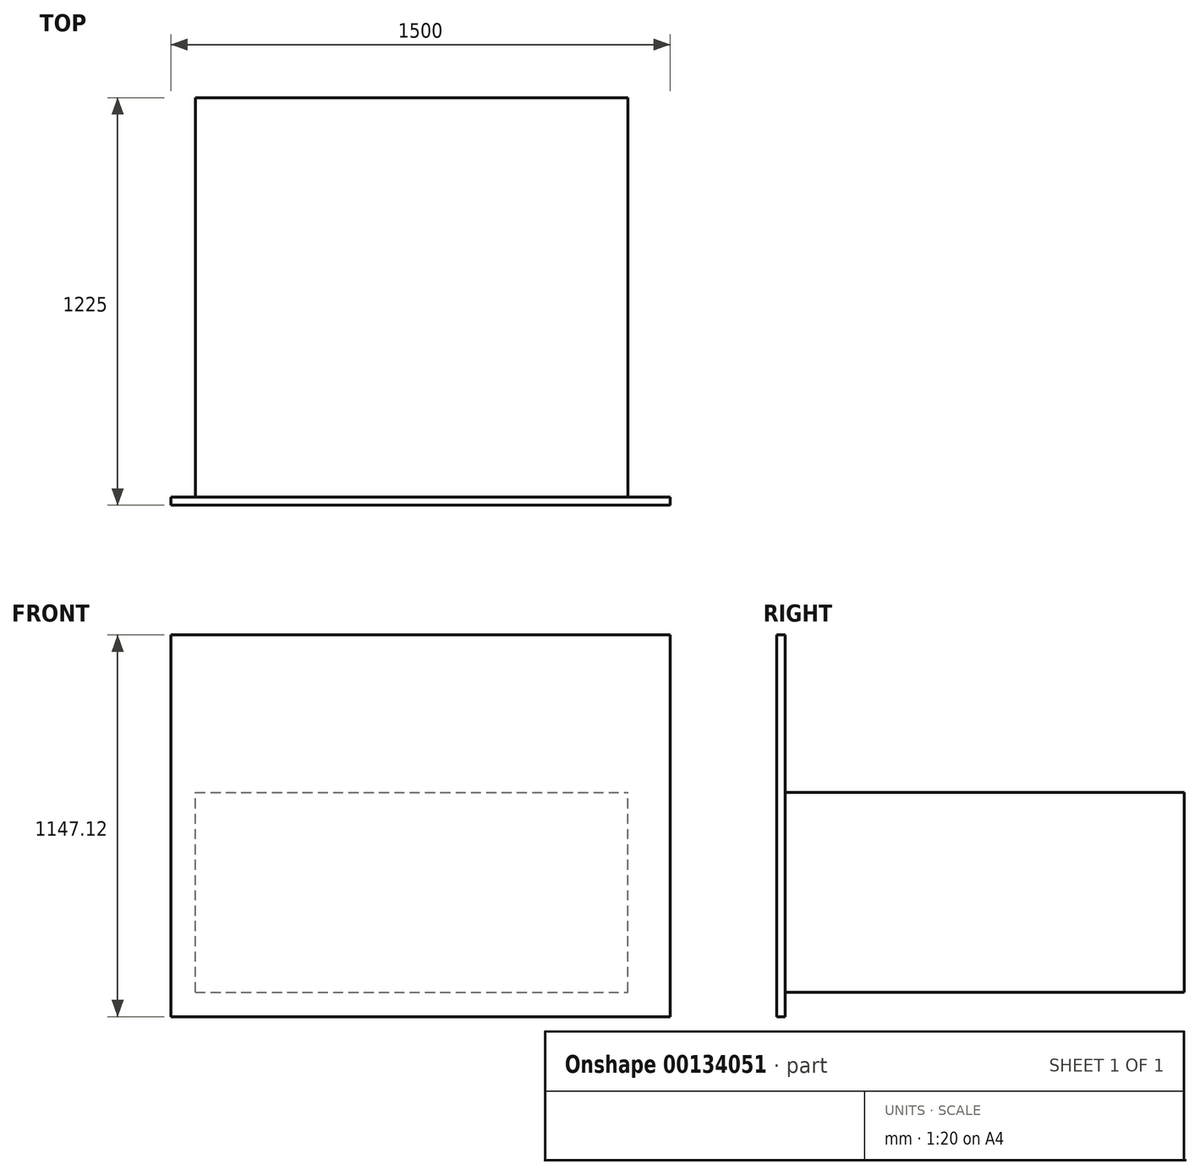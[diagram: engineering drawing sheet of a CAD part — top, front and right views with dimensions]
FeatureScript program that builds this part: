
annotation { "Feature Type Name" : "Feature", "Feature Type Description" : "" }
export const myFeature = defineFeature(function(context is Context, id is Id, definition is map)
    precondition{}
    {
        {
            var Q0;
            Q0=qCreatedBy(makeId("Front.planeOp"),FACE);
            var sketch = newSketch(context, id + "F0", { "sketchPlane" : qUnion([Q0])});
            skLineSegment(sketch, "E0.bottom", {"start": v(0, 0) * mm, "end": v(1300, 0) * mm});
            skLineSegment(sketch, "E0.top", {"start": v(0, 600) * mm, "end": v(1300, 600) * mm});
            skLineSegment(sketch, "E0.left", {"start": v(0, 0) * mm, "end": v(0, 600) * mm});
            skLineSegment(sketch, "E0.right", {"start": v(1300, 0) * mm, "end": v(1300, 600) * mm});
            skSolve(sketch);
        }
        {
            var Q0;
            Q0=makeQuery(id+"F0.imprint","IMPRINT",FACE,{"disambiguationData":[TD([[makeQuery(id+"F0.imprint","IMPRINT",EDGE,{"derivedFrom":sQuery(id+"F0.wireOp",EDGE,"E0.bottom")}),1.0]])]});
            extrude(context, id + "F1", {"entities" : qUnion([Q0]), "depth" : 1200 * mm});
        }
        {
            var Q0;
            Q0=makeQuery(id+"F1.opExtrude","CAP_FACE",FACE,{"disambiguationData":[OSD([sQuery(id+"F0.wireOp",EDGE,"E0.bottom"),sQuery(id+"F0.wireOp",EDGE,"E0.top"),sQuery(id+"F0.wireOp",EDGE,"E0.left"),sQuery(id+"F0.wireOp",EDGE,"E0.right")])],"isStart":false});
            var sketch = newSketch(context, id + "F2", { "sketchPlane" : qUnion([Q0])});
            skLineSegment(sketch, "E1.0", {"start": v(-73.56, 1073.56) * mm, "end": v(-73.56, -73.56) * mm});
            skLineSegment(sketch, "E2", {"start": v(-73.56, 1073.56) * mm, "end": v(1426.44, 1073.56) * mm});
            skLineSegment(sketch, "E3", {"start": v(1426.44, 1073.56) * mm, "end": v(1426.44, -73.56) * mm});
            skLineSegment(sketch, "E4", {"start": v(1426.44, -73.56) * mm, "end": v(-73.56, -73.56) * mm});
            skSolve(sketch);
        }
        {
            var Q0;
            Q0=makeQuery(id+"F2.imprint","IMPRINT",FACE,{"disambiguationData":[TD([[makeQuery(id+"F2.imprint","IMPRINT",EDGE,{"derivedFrom":makeQuery(id+"F1.opExtrude","CAP_EDGE",EDGE,{"disambiguationData":[OSD([sQuery(id+"F0.wireOp",EDGE,"E0.bottom")])],"isStart":false})}),1.0]])]});
            var Q1;
            Q1=makeQuery(id+"F2.imprint","IMPRINT",FACE,{"disambiguationData":[TD([[makeQuery(id+"F2.imprint","IMPRINT",EDGE,{"derivedFrom":sQuery(id+"F2.wireOp",EDGE,"E1.0")}),1.0]])]});
            extrude(context, id + "F3", {"entities" : qUnion([Q0, Q1]), "operationType" : NewBodyOperationType.ADD, "depth" : 25 * mm});
        }
    });
